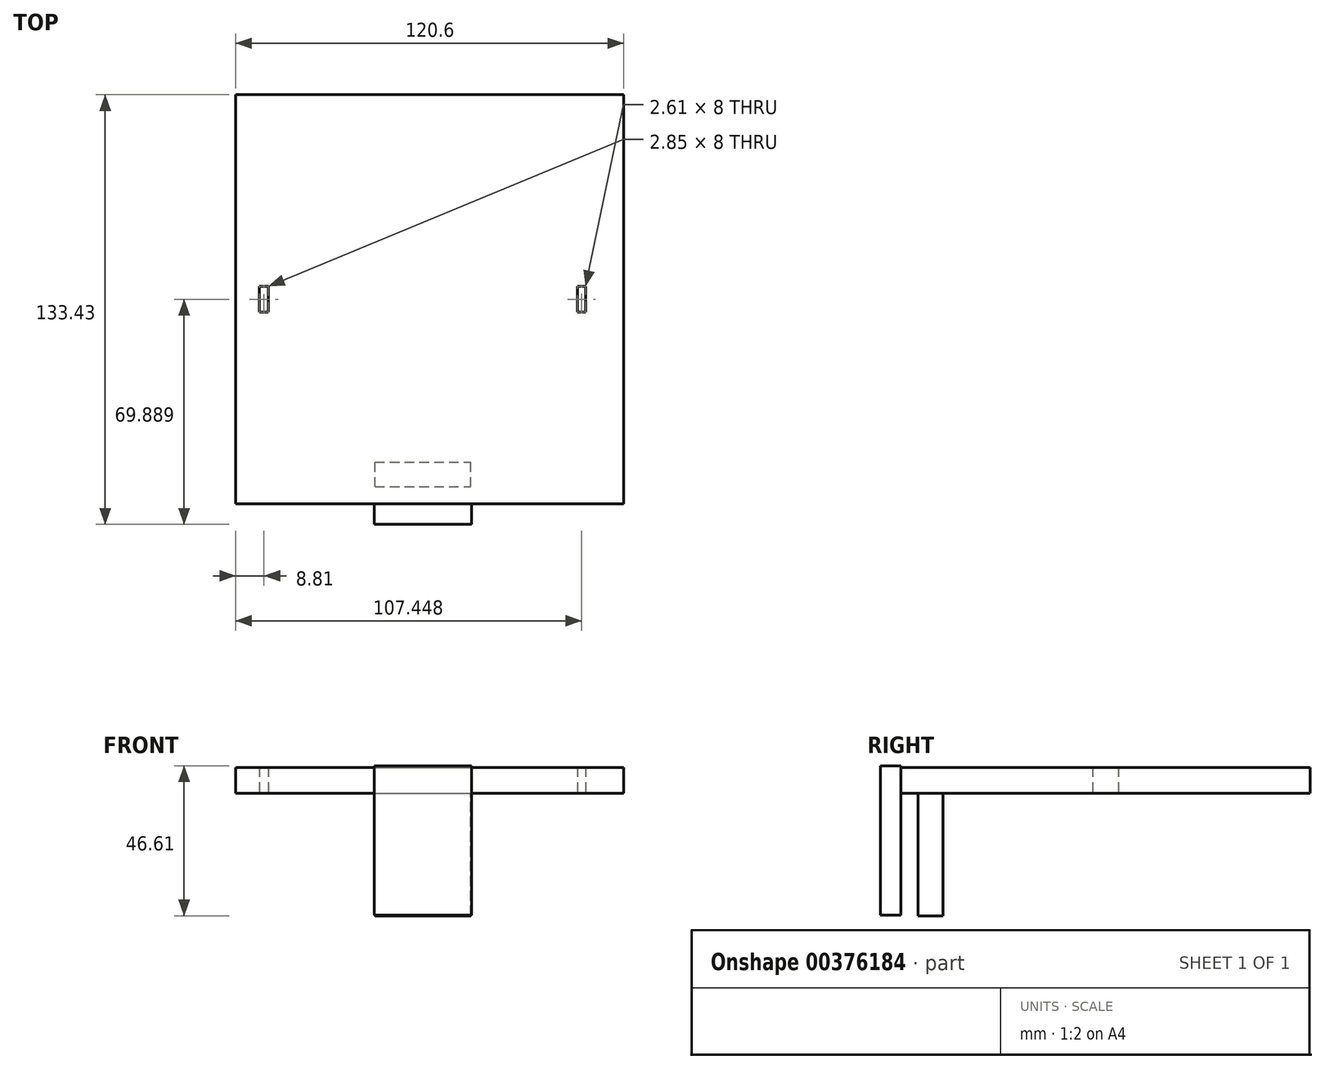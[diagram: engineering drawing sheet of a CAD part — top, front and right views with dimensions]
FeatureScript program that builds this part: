
annotation { "Feature Type Name" : "Feature", "Feature Type Description" : "" }
export const myFeature = defineFeature(function(context is Context, id is Id, definition is map)
    precondition{}
    {
        {
            var Q0;
            Q0=qCreatedBy(makeId("Top.planeOp"),FACE);
            var sketch = newSketch(context, id + "F0", { "sketchPlane" : qUnion([Q0])});
            skLineSegment(sketch, "E0.bottom", {"start": v(-47.23, 58.82) * mm, "end": v(73.37, 58.82) * mm});
            skLineSegment(sketch, "E0.top", {"start": v(-47.23, -68.26) * mm, "end": v(73.37, -68.26) * mm});
            skLineSegment(sketch, "E0.left", {"start": v(-47.23, 58.82) * mm, "end": v(-47.23, -68.26) * mm});
            skLineSegment(sketch, "E0.right", {"start": v(73.37, 58.82) * mm, "end": v(73.37, -68.26) * mm});
            skLineSegment(sketch, "E1.bottom", {"start": v(-39.84, -0.72) * mm, "end": v(-37, -0.72) * mm});
            skLineSegment(sketch, "E1.top", {"start": v(-39.84, -8.72) * mm, "end": v(-37, -8.72) * mm});
            skLineSegment(sketch, "E1.left", {"start": v(-39.84, -0.72) * mm, "end": v(-39.84, -8.72) * mm});
            skLineSegment(sketch, "E1.right", {"start": v(-37, -0.72) * mm, "end": v(-37, -8.72) * mm});
            skLineSegment(sketch, "E2", {"start": v(0, 58.82) * mm, "end": v(0, -68.26) * mm});
            skLineSegment(sketch, "E3", {"start": v(0, -68.26) * mm, "end": v(0, 52.8) * mm, "construction": true});
            skLineSegment(sketch, "E4.bottom", {"start": v(58.91, -0.72) * mm, "end": v(61.52, -0.72) * mm});
            skLineSegment(sketch, "E4.top", {"start": v(58.91, -8.72) * mm, "end": v(61.52, -8.72) * mm});
            skLineSegment(sketch, "E4.left", {"start": v(58.91, -0.72) * mm, "end": v(58.91, -8.72) * mm});
            skLineSegment(sketch, "E4.right", {"start": v(61.52, -0.72) * mm, "end": v(61.52, -8.72) * mm});
            skSolve(sketch);
        }
        {
            var Q0;
            Q0 = qSketchRegion(id + "F0", true);
            extrude(context, id + "F1", {"entities" : qUnion([Q0]), "depth" : 7.98 * mm});
        }
        {
            var Q0;
            Q0=makeQuery(id+"F1.opExtrude","SWEPT_FACE",FACE,{"disambiguationData":[OSD([sQuery(id+"F0.wireOp",EDGE,"E0.top")])]});
            cPlane(context, id + "F2", {"entities" : qUnion([Q0]), "cplaneType" : CPlaneType.OFFSET, "offset" : 0 * mm, "width" : 152.4 * mm, "height" : 152.4 * mm});
        }
        {
            var Q0;
            Q0=qCreatedBy(id+"F2.planeOp",FACE);
            var sketch = newSketch(context, id + "F3", { "sketchPlane" : qUnion([Q0])});
            skLineSegment(sketch, "E5.bottom", {"start": v(-4.1, 8.5) * mm, "end": v(26.02, 8.5) * mm});
            skLineSegment(sketch, "E5.top", {"start": v(-4.1, -37.89) * mm, "end": v(26.02, -37.89) * mm});
            skLineSegment(sketch, "E5.left", {"start": v(-4.1, 8.5) * mm, "end": v(-4.1, -37.89) * mm});
            skLineSegment(sketch, "E5.right", {"start": v(26.02, 8.5) * mm, "end": v(26.02, -37.89) * mm});
            skSolve(sketch);
        }
        {
            var Q0;
            Q0=makeQuery(id+"F3.imprint","IMPRINT",FACE,{"disambiguationData":[TD([[makeQuery(id+"F3.imprint","IMPRINT",EDGE,{"derivedFrom":sQuery(id+"F3.wireOp",EDGE,"E5.bottom")}),-1.0]])]});
            extrude(context, id + "F4", {"entities" : qUnion([Q0]), "operationType" : NewBodyOperationType.ADD, "depth" : 6.35 * mm});
        }
        {
            var Q0;
            Q0=makeQuery(id+"F1.opExtrude","CAP_FACE",FACE,{"disambiguationData":[OSD([sQuery(id+"F0.wireOp",EDGE,"E0.bottom"),sQuery(id+"F0.wireOp",EDGE,"E0.top"),sQuery(id+"F0.wireOp",EDGE,"E0.left"),sQuery(id+"F0.wireOp",EDGE,"E0.right"),sQuery(id+"F0.wireOp",EDGE,"E1.bottom"),sQuery(id+"F0.wireOp",EDGE,"E1.top"),sQuery(id+"F0.wireOp",EDGE,"E1.left"),sQuery(id+"F0.wireOp",EDGE,"E1.right"),sQuery(id+"F0.wireOp",EDGE,"E4.bottom"),sQuery(id+"F0.wireOp",EDGE,"E4.top"),sQuery(id+"F0.wireOp",EDGE,"E4.left"),sQuery(id+"F0.wireOp",EDGE,"E4.right")])],"isStart":true});
            cPlane(context, id + "F5", {"entities" : qUnion([Q0]), "cplaneType" : CPlaneType.OFFSET, "offset" : 0 * mm, "width" : 152.4 * mm, "height" : 152.4 * mm});
        }
        {
            var Q0;
            Q0=qCreatedBy(id+"F5.planeOp",FACE);
            var sketch = newSketch(context, id + "F6", { "sketchPlane" : qUnion([Q0])});
            skLineSegment(sketch, "E6.bottom", {"start": v(6.45, 62.96) * mm, "end": v(16.14, 62.96) * mm});
            skLineSegment(sketch, "E6.top", {"start": v(6.45, 60.09) * mm, "end": v(16.14, 60.09) * mm});
            skLineSegment(sketch, "E6.left", {"start": v(6.45, 62.96) * mm, "end": v(6.45, 60.09) * mm});
            skLineSegment(sketch, "E6.right", {"start": v(16.14, 62.96) * mm, "end": v(16.14, 60.09) * mm});
            skPoint(sketch, "E7.firstSnap0", {"position": v(11.3, 62.96) * mm});
            skLineSegment(sketch, "E7.bottom", {"start": v(-3.93, 62.96) * mm, "end": v(25.8, 62.96) * mm});
            skLineSegment(sketch, "E7.top", {"start": v(-3.93, 55.26) * mm, "end": v(25.8, 55.26) * mm});
            skLineSegment(sketch, "E7.left", {"start": v(-3.93, 62.96) * mm, "end": v(-3.93, 55.26) * mm});
            skLineSegment(sketch, "E7.right", {"start": v(25.8, 62.96) * mm, "end": v(25.8, 55.26) * mm});
            skSolve(sketch);
        }
        {
            var Q0;
            Q0 = qSketchRegion(id + "F6", true);
            extrude(context, id + "F7", {"entities" : qUnion([Q0]), "operationType" : NewBodyOperationType.ADD, "depth" : 25.4 * mm});
        }
        {
            var Q0;
            Q0=makeQuery(id+"F7.opExtrude","CAP_FACE",FACE,{"disambiguationData":[OSD([sQuery(id+"F6.wireOp",EDGE,"E7.bottom"),sQuery(id+"F6.wireOp",EDGE,"E7.top"),sQuery(id+"F6.wireOp",EDGE,"E7.left"),sQuery(id+"F6.wireOp",EDGE,"E7.right")])],"isStart":false});
            extrude(context, id + "F8", {"entities" : qUnion([Q0]), "operationType" : NewBodyOperationType.ADD, "depth" : 12.7 * mm});
        }
    });
